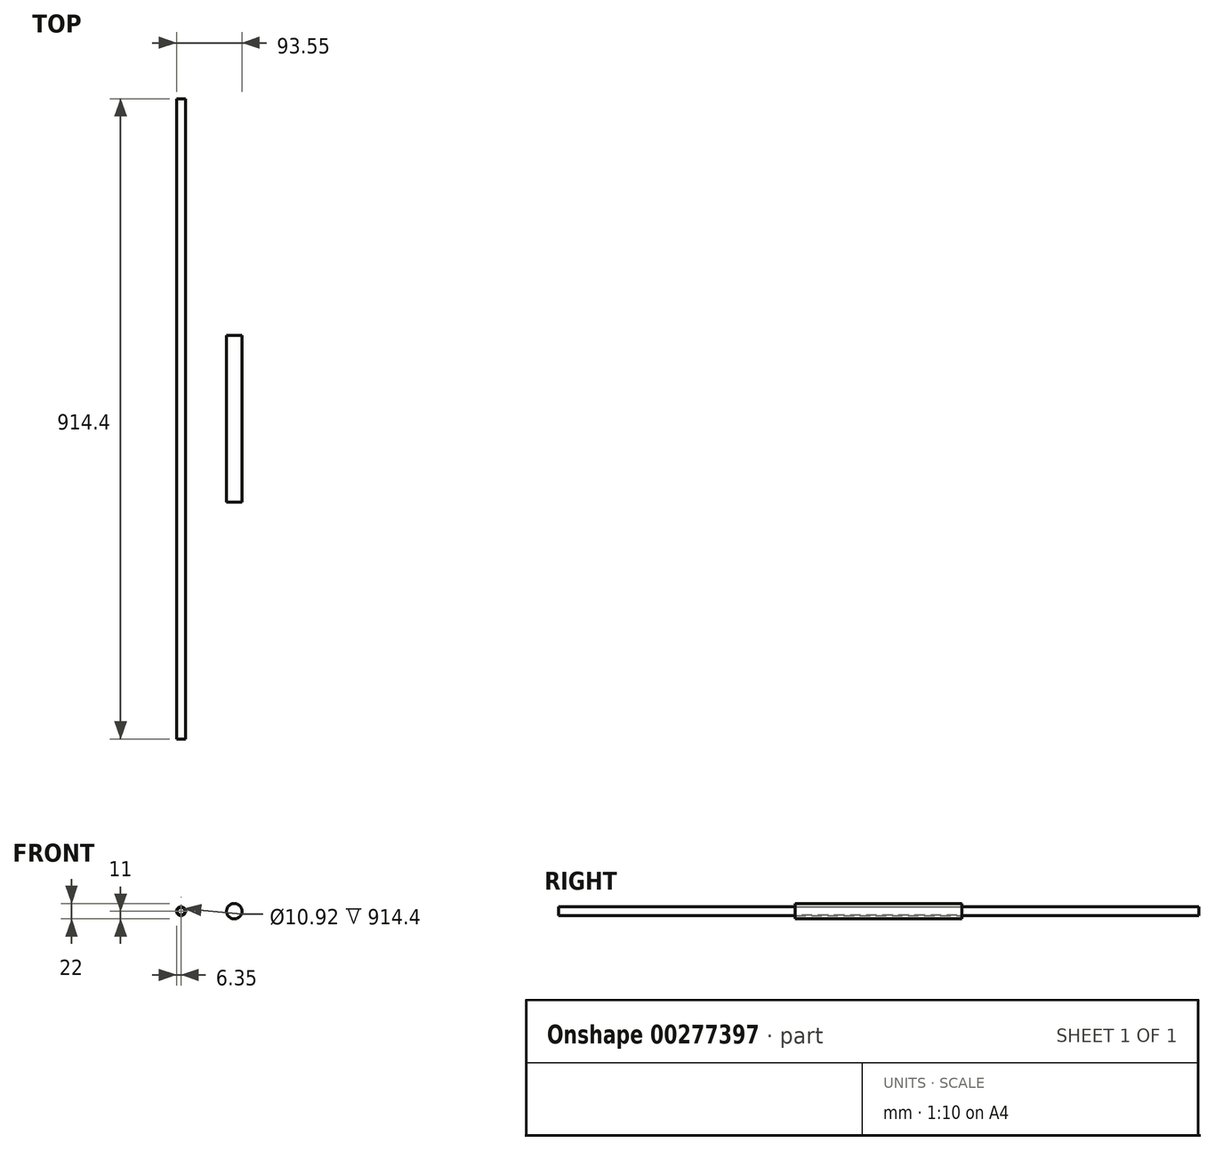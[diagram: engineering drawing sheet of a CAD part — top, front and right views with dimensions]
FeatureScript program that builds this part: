
annotation { "Feature Type Name" : "Feature", "Feature Type Description" : "" }
export const myFeature = defineFeature(function(context is Context, id is Id, definition is map)
    precondition{}
    {
        {
            var Q0;
            Q0=qCreatedBy(makeId("Front.planeOp"),FACE);
            var sketch = newSketch(context, id + "F0", { "sketchPlane" : qUnion([Q0])});
            skCircle(sketch, "E0", {"center": v(0, 0) * mm, "radius": 11 * mm});
            skSolve(sketch);
        }
        {
            var Q0;
            Q0 = qSketchRegion(id + "F0", true);
            extrude(context, id + "F1", {"entities" : qUnion([Q0]), "endBound" : BoundingType.SYMMETRIC, "depth" : 238.12 * mm});
        }
        {
            var Q0;
            Q0=qCreatedBy(makeId("Front.planeOp"),FACE);
            var sketch = newSketch(context, id + "F2", { "sketchPlane" : qUnion([Q0])});
            skCircle(sketch, "E1", {"center": v(-76.2, 0) * mm, "radius": 6.35 * mm});
            skSolve(sketch);
        }
        {
            var Q0;
            Q0 = qSketchRegion(id + "F2", true);
            extrude(context, id + "F3", {"entities" : qUnion([Q0]), "endBound" : BoundingType.SYMMETRIC, "depth" : 914.4 * mm});
        }
        {
            var Q0;
            Q0=makeQuery(id+"F3.opExtrude","CAP_FACE",FACE,{"disambiguationData":[OSD([sQuery(id+"F2.wireOp",EDGE,"E1")])],"isStart":false});
            var sketch = newSketch(context, id + "F4", { "sketchPlane" : qUnion([Q0])});
            skCircle(sketch, "E2", {"center": v(-76.2, 0) * mm, "radius": 5.46 * mm});
            skSolve(sketch);
        }
        {
            var Q0;
            Q0 = qSketchRegion(id + "F4", true);
            extrude(context, id + "F5", {"entities" : qUnion([Q0]), "operationType" : NewBodyOperationType.REMOVE, "endBound" : BoundingType.THROUGH_ALL, "oppositeDirection" : true, "depth" : 25.4 * mm});
        }
    });
